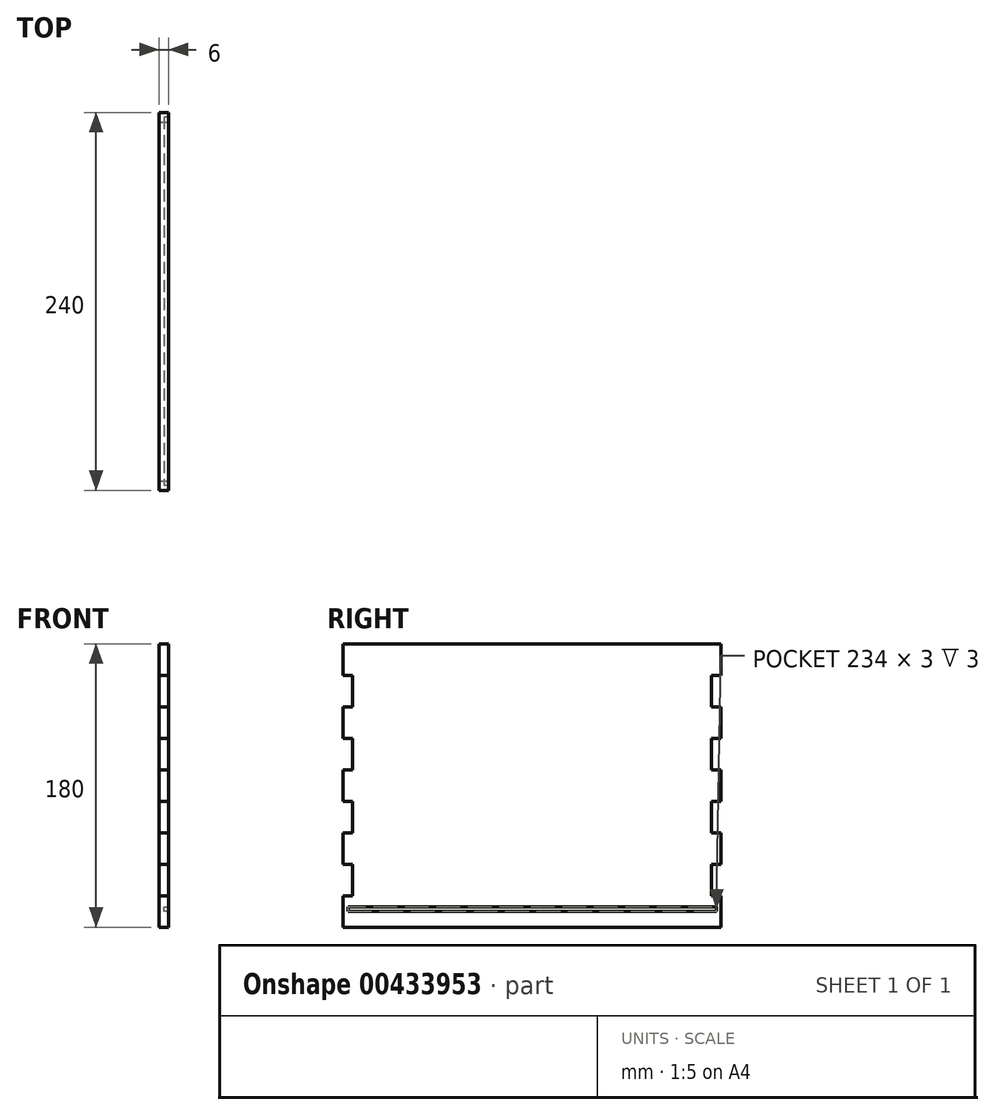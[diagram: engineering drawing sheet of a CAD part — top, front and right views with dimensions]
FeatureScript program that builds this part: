
annotation { "Feature Type Name" : "Feature", "Feature Type Description" : "" }
export const myFeature = defineFeature(function(context is Context, id is Id, definition is map)
    precondition{}
    {
        {
            var Q0;
            Q0=qCreatedBy(makeId("Top.planeOp"),FACE);
            var sketch = newSketch(context, id + "F0", { "sketchPlane" : qUnion([Q0])});
            skLineSegment(sketch, "E0.bottom", {"start": v(-3, -120) * mm, "end": v(3, -120) * mm});
            skLineSegment(sketch, "E0.top", {"start": v(-3, 120) * mm, "end": v(3, 120) * mm});
            skLineSegment(sketch, "E0.left", {"start": v(-3, -120) * mm, "end": v(-3, 120) * mm});
            skLineSegment(sketch, "E0.right", {"start": v(3, -120) * mm, "end": v(3, 120) * mm});
            skPoint(sketch, "E0.middle", {"position": v(0, 0) * mm});
            skSolve(sketch);
        }
        {
            var Q0;
            Q0=makeQuery(id+"F0.imprint","IMPRINT",FACE,{"disambiguationData":[TD([[makeQuery(id+"F0.imprint","IMPRINT",EDGE,{"derivedFrom":sQuery(id+"F0.wireOp",EDGE,"E0.bottom")}),1.0]])]});
            extrude(context, id + "F1", {"entities" : qUnion([Q0]), "depth" : 180 * mm});
        }
        {
            var Q0;
            Q0=makeQuery(id+"F1.opExtrude","SWEPT_FACE",FACE,{"disambiguationData":[OSD([sQuery(id+"F0.wireOp",EDGE,"E0.bottom")])]});
            var sketch = newSketch(context, id + "F2", { "sketchPlane" : qUnion([Q0])});
            skLineSegment(sketch, "E1", {"start": v(3, 10) * mm, "end": v(0, 10) * mm});
            skLineSegment(sketch, "E2", {"start": v(3, 13) * mm, "end": v(3, 10) * mm});
            skLineSegment(sketch, "E3", {"start": v(0, 10) * mm, "end": v(0, 13) * mm});
            skLineSegment(sketch, "E4", {"start": v(0, 13) * mm, "end": v(3, 13) * mm});
            skSolve(sketch);
        }
        {
            var Q0;
            Q0=makeQuery(id+"F2.imprint","IMPRINT",FACE,{"disambiguationData":[TD([[makeQuery(id+"F2.imprint","IMPRINT",EDGE,{"derivedFrom":sQuery(id+"F2.wireOp",EDGE,"E1")}),-1.0]])]});
            var Q1;
            Q1=qCreatedBy(makeId("Front.planeOp"),FACE);
            extrude(context, id + "F3", {"entities" : qUnion([Q0]), "operationType" : NewBodyOperationType.REMOVE, "oppositeDirection" : true, "endBoundEntityFace" : qUnion([Q1]), "depth" : 237 * mm, "hasSecondDirection" : true, "secondDirectionOppositeDirection" : true, "secondDirectionDepth" : 3 * mm});
        }
        {
            var Q0;
            Q0=makeQuery(id+"F1.opExtrude","SWEPT_FACE",FACE,{"disambiguationData":[OSD([sQuery(id+"F0.wireOp",EDGE,"E0.right")])]});
            var sketch = newSketch(context, id + "F4", { "sketchPlane" : qUnion([Q0])});
            skLineSegment(sketch, "E5", {"start": v(-120, 20) * mm, "end": v(-114, 20) * mm});
            skLineSegment(sketch, "E6", {"start": v(-114, 20) * mm, "end": v(-114, 40) * mm});
            skLineSegment(sketch, "E7", {"start": v(-114, 40) * mm, "end": v(-120, 40) * mm});
            skLineSegment(sketch, "E8.1.0.0", {"start": v(-114, 80) * mm, "end": v(-120, 80) * mm});
            skLineSegment(sketch, "E8.1.0.1", {"start": v(-114, 60) * mm, "end": v(-114, 80) * mm});
            skLineSegment(sketch, "E8.1.0.2", {"start": v(-120, 60) * mm, "end": v(-114, 60) * mm});
            skLineSegment(sketch, "E8.2.0.0", {"start": v(-114, 120) * mm, "end": v(-120, 120) * mm});
            skLineSegment(sketch, "E8.2.0.1", {"start": v(-114, 100) * mm, "end": v(-114, 120) * mm});
            skLineSegment(sketch, "E8.2.0.2", {"start": v(-120, 100) * mm, "end": v(-114, 100) * mm});
            skLineSegment(sketch, "E8.3.0.0", {"start": v(-114, 160) * mm, "end": v(-120, 160) * mm});
            skLineSegment(sketch, "E8.3.0.1", {"start": v(-114, 140) * mm, "end": v(-114, 160) * mm});
            skLineSegment(sketch, "E8.3.0.2", {"start": v(-120, 140) * mm, "end": v(-114, 140) * mm});
            skLineSegment(sketch, "E8.4.0.0", {"start": v(-114, 200) * mm, "end": v(-120, 200) * mm});
            skLineSegment(sketch, "E8.4.0.1", {"start": v(-114, 180) * mm, "end": v(-114, 200) * mm});
            skLineSegment(sketch, "E8.4.0.2", {"start": v(-120, 180) * mm, "end": v(-114, 180) * mm});
            skLineSegment(sketch, "E8.direction1", {"start": v(-120, 40) * mm, "end": v(-120, 80) * mm, "construction": true});
            skLineSegment(sketch, "E9.MirrorCS", {"start": v(114, 40) * mm, "end": v(120, 40) * mm});
            skLineSegment(sketch, "E10.MirrorCS", {"start": v(120, 140) * mm, "end": v(114, 140) * mm});
            skLineSegment(sketch, "E11.MirrorCS", {"start": v(114, 80) * mm, "end": v(120, 80) * mm});
            skLineSegment(sketch, "E12.MirrorCS", {"start": v(120, 60) * mm, "end": v(114, 60) * mm});
            skLineSegment(sketch, "E13.MirrorCS", {"start": v(120, 100) * mm, "end": v(114, 100) * mm});
            skLineSegment(sketch, "E14.MirrorCS", {"start": v(114, 160) * mm, "end": v(120, 160) * mm});
            skLineSegment(sketch, "E15.MirrorCS", {"start": v(114, 200) * mm, "end": v(120, 200) * mm});
            skLineSegment(sketch, "E16.MirrorCS", {"start": v(120, 180) * mm, "end": v(114, 180) * mm});
            skLineSegment(sketch, "E17.MirrorCS", {"start": v(120, 20) * mm, "end": v(114, 20) * mm});
            skLineSegment(sketch, "E18.MirrorCS", {"start": v(114, 120) * mm, "end": v(120, 120) * mm});
            skLineSegment(sketch, "E19.MirrorCS", {"start": v(114, 180) * mm, "end": v(114, 200) * mm});
            skLineSegment(sketch, "E20.MirrorCS", {"start": v(120, 40) * mm, "end": v(120, 80) * mm, "construction": true});
            skLineSegment(sketch, "E21.MirrorCS", {"start": v(114, 20) * mm, "end": v(114, 40) * mm});
            skLineSegment(sketch, "E22.MirrorCS", {"start": v(114, 60) * mm, "end": v(114, 80) * mm});
            skLineSegment(sketch, "E23.MirrorCS", {"start": v(114, 100) * mm, "end": v(114, 120) * mm});
            skLineSegment(sketch, "E24.MirrorCS", {"start": v(114, 140) * mm, "end": v(114, 160) * mm});
            skSolve(sketch);
        }
        {
            var Q0;
            {var subQ0=sQuery(id+"F4.wireOp",EDGE,"E5");Q0=makeQuery(id+"F4.imprint","IMPRINT",FACE,{"disambiguationData":[TD([[makeQuery(id+"F4.imprint","IMPRINT",EDGE,{"derivedFrom":subQ0}),1.0]])]});}
            var Q1;
            {var subQ0=sQuery(id+"F4.wireOp",EDGE,"E8.1.0.0");Q1=makeQuery(id+"F4.imprint","IMPRINT",FACE,{"disambiguationData":[TD([[makeQuery(id+"F4.imprint","IMPRINT",EDGE,{"derivedFrom":subQ0}),1.0]])]});}
            var Q2;
            {var subQ0=sQuery(id+"F4.wireOp",EDGE,"E8.2.0.0");Q2=makeQuery(id+"F4.imprint","IMPRINT",FACE,{"disambiguationData":[TD([[makeQuery(id+"F4.imprint","IMPRINT",EDGE,{"derivedFrom":subQ0}),1.0]])]});}
            var Q3;
            {var subQ0=sQuery(id+"F4.wireOp",EDGE,"E8.3.0.0");Q3=makeQuery(id+"F4.imprint","IMPRINT",FACE,{"disambiguationData":[TD([[makeQuery(id+"F4.imprint","IMPRINT",EDGE,{"derivedFrom":subQ0}),1.0]])]});}
            var Q4;
            {var subQ0=sQuery(id+"F4.wireOp",EDGE,"E8.4.0.0");Q4=makeQuery(id+"F4.imprint","IMPRINT",FACE,{"disambiguationData":[TD([[makeQuery(id+"F4.imprint","IMPRINT",EDGE,{"derivedFrom":subQ0}),-1.0]])]});}
            var Q5;
            {var subQ0=sQuery(id+"F4.wireOp",EDGE,"E15.MirrorCS");Q5=makeQuery(id+"F4.imprint","IMPRINT",FACE,{"disambiguationData":[TD([[makeQuery(id+"F4.imprint","IMPRINT",EDGE,{"derivedFrom":subQ0}),-1.0]])]});}
            var Q6;
            {var subQ0=sQuery(id+"F4.wireOp",EDGE,"E10.MirrorCS");Q6=makeQuery(id+"F4.imprint","IMPRINT",FACE,{"disambiguationData":[TD([[makeQuery(id+"F4.imprint","IMPRINT",EDGE,{"derivedFrom":subQ0}),-1.0]])]});}
            var Q7;
            {var subQ0=sQuery(id+"F4.wireOp",EDGE,"E13.MirrorCS");Q7=makeQuery(id+"F4.imprint","IMPRINT",FACE,{"disambiguationData":[TD([[makeQuery(id+"F4.imprint","IMPRINT",EDGE,{"derivedFrom":subQ0}),-1.0]])]});}
            var Q8;
            {var subQ0=sQuery(id+"F4.wireOp",EDGE,"E11.MirrorCS");Q8=makeQuery(id+"F4.imprint","IMPRINT",FACE,{"disambiguationData":[TD([[makeQuery(id+"F4.imprint","IMPRINT",EDGE,{"derivedFrom":subQ0}),-1.0]])]});}
            var Q9;
            {var subQ0=sQuery(id+"F4.wireOp",EDGE,"E9.MirrorCS");Q9=makeQuery(id+"F4.imprint","IMPRINT",FACE,{"disambiguationData":[TD([[makeQuery(id+"F4.imprint","IMPRINT",EDGE,{"derivedFrom":subQ0}),-1.0]])]});}
            extrude(context, id + "F5", {"entities" : qUnion([Q0, Q1, Q2, Q3, Q4, Q5, Q6, Q7, Q8, Q9]), "operationType" : NewBodyOperationType.REMOVE, "endBound" : BoundingType.THROUGH_ALL, "oppositeDirection" : true, "depth" : 25 * mm});
        }
    });
